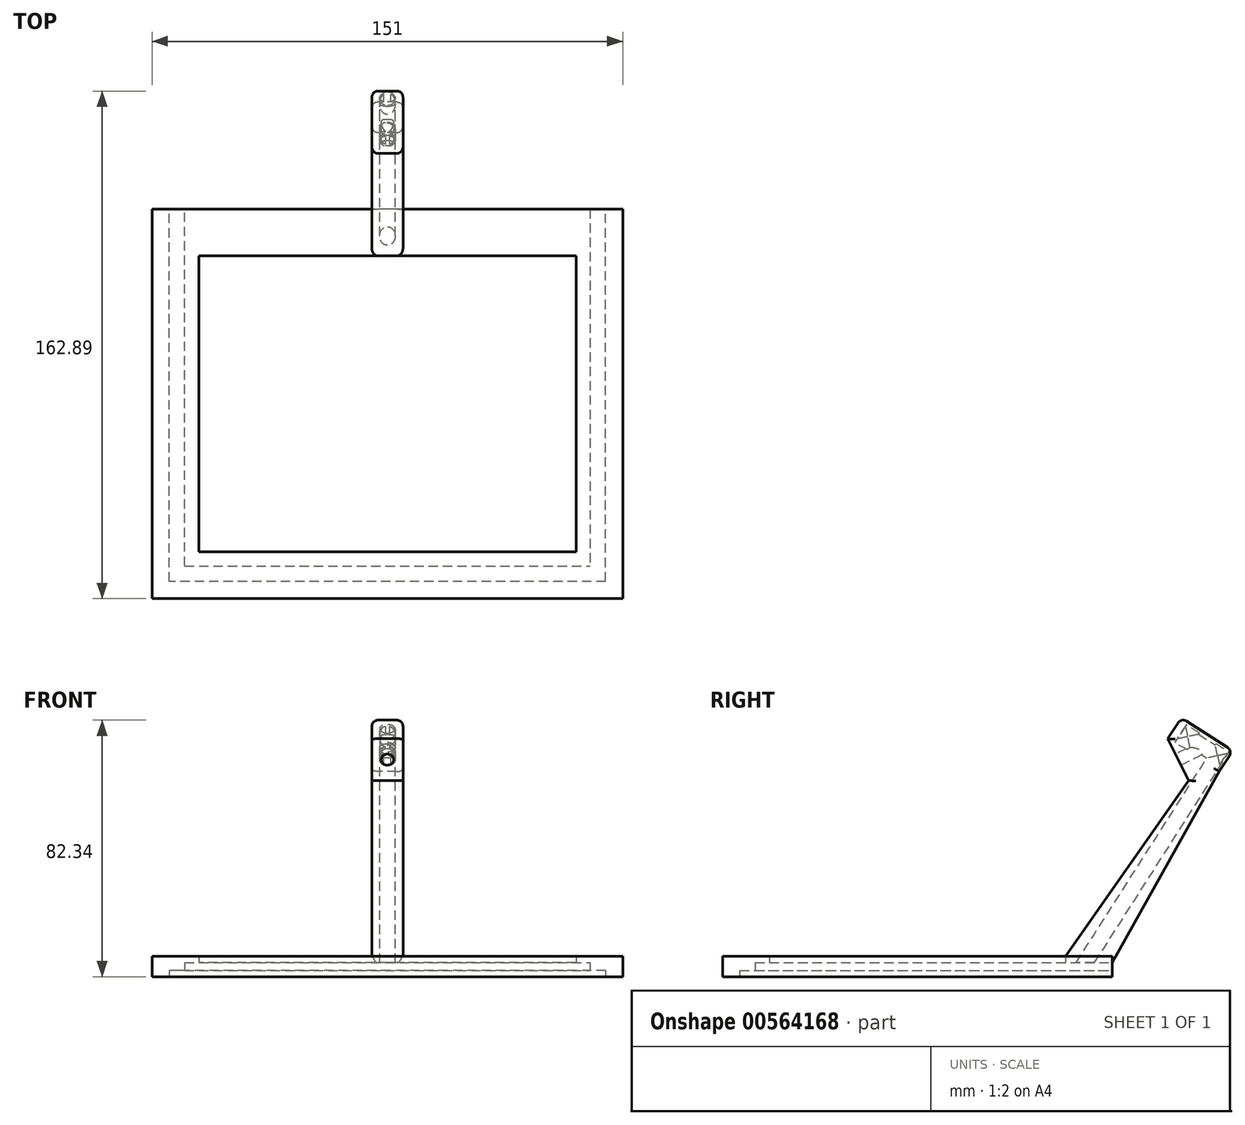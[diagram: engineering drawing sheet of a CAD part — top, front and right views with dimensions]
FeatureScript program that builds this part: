
annotation { "Feature Type Name" : "Feature", "Feature Type Description" : "" }
export const myFeature = defineFeature(function(context is Context, id is Id, definition is map)
    precondition{}
    {
        {
            var Q0;
            Q0=qCreatedBy(makeId("Top.planeOp"),FACE);
            var sketch = newSketch(context, id + "F0", { "sketchPlane" : qUnion([Q0])});
            skLineSegment(sketch, "E0.bottom", {"start": v(60.5, -47.5) * mm, "end": v(-60.5, -47.5) * mm});
            skLineSegment(sketch, "E0.top", {"start": v(60.5, 47.5) * mm, "end": v(-60.5, 47.5) * mm});
            skLineSegment(sketch, "E0.left", {"start": v(60.5, -47.5) * mm, "end": v(60.5, 47.5) * mm});
            skLineSegment(sketch, "E0.right", {"start": v(-60.5, -47.5) * mm, "end": v(-60.5, 47.5) * mm});
            skPoint(sketch, "E0.middle", {"position": v(0, 0) * mm});
            skLineSegment(sketch, "E1.bottom", {"start": v(75.5, -62.5) * mm, "end": v(-75.5, -62.5) * mm});
            skLineSegment(sketch, "E1.top", {"start": v(75.5, 62.5) * mm, "end": v(-75.5, 62.5) * mm});
            skLineSegment(sketch, "E1.left", {"start": v(75.5, -62.5) * mm, "end": v(75.5, 62.5) * mm});
            skLineSegment(sketch, "E1.right", {"start": v(-75.5, -62.5) * mm, "end": v(-75.5, 62.5) * mm});
            skSolve(sketch);
        }
        {
            var Q0;
            Q0=makeQuery(id+"F0.imprint","IMPRINT",FACE,{"disambiguationData":[TD([[makeQuery(id+"F0.imprint","IMPRINT",EDGE,{"derivedFrom":sQuery(id+"F0.wireOp",EDGE,"E0.bottom")}),1.0]])]});
            extrude(context, id + "F1", {"entities" : qUnion([Q0]), "depth" : 5 * mm, "offsetDistance" : 25 * mm});
        }
        {
            var Q0;
            Q0=makeQuery(id+"F1.opExtrude","CAP_FACE",FACE,{"disambiguationData":[OSD([sQuery(id+"F0.wireOp",EDGE,"E0.bottom"),sQuery(id+"F0.wireOp",EDGE,"E0.top"),sQuery(id+"F0.wireOp",EDGE,"E0.left"),sQuery(id+"F0.wireOp",EDGE,"E0.right"),sQuery(id+"F0.wireOp",EDGE,"E1.bottom"),sQuery(id+"F0.wireOp",EDGE,"E1.top"),sQuery(id+"F0.wireOp",EDGE,"E1.left"),sQuery(id+"F0.wireOp",EDGE,"E1.right")])],"isStart":true});
            var sketch = newSketch(context, id + "F2", { "sketchPlane" : qUnion([Q0])});
            skLineSegment(sketch, "E2.bottom", {"start": v(-65, 52) * mm, "end": v(65, 52) * mm});
            skLineSegment(sketch, "E2.top", {"start": v(-65, -52) * mm, "end": v(65, -52) * mm});
            skLineSegment(sketch, "E2.left", {"start": v(-65, 52) * mm, "end": v(-65, -52) * mm});
            skLineSegment(sketch, "E2.right", {"start": v(65, 52) * mm, "end": v(65, -52) * mm});
            skPoint(sketch, "E2.middle", {"position": v(0, 0) * mm});
            skSolve(sketch);
        }
        {
            var Q0;
            Q0=makeQuery(id+"F2.imprint","IMPRINT",FACE,{"disambiguationData":[TD([[makeQuery(id+"F2.imprint","IMPRINT",EDGE,{"derivedFrom":sQuery(id+"F2.wireOp",EDGE,"E2.bottom")}),-1.0]])]});
            extrude(context, id + "F3", {"entities" : qUnion([Q0]), "operationType" : NewBodyOperationType.REMOVE, "oppositeDirection" : true, "depth" : 3 * mm, "offsetDistance" : 25 * mm});
        }
        {
            var Q0;
            Q0=makeQuery(id+"F1.opExtrude","CAP_FACE",FACE,{"disambiguationData":[OSD([sQuery(id+"F0.wireOp",EDGE,"E0.bottom"),sQuery(id+"F0.wireOp",EDGE,"E0.top"),sQuery(id+"F0.wireOp",EDGE,"E0.left"),sQuery(id+"F0.wireOp",EDGE,"E0.right"),sQuery(id+"F0.wireOp",EDGE,"E1.bottom"),sQuery(id+"F0.wireOp",EDGE,"E1.top"),sQuery(id+"F0.wireOp",EDGE,"E1.left"),sQuery(id+"F0.wireOp",EDGE,"E1.right")])],"isStart":true});
            var sketch = newSketch(context, id + "F4", { "sketchPlane" : qUnion([Q0])});
            skLineSegment(sketch, "E3.bottom", {"start": v(75.5, 62.5) * mm, "end": v(-75.5, 62.5) * mm});
            skLineSegment(sketch, "E3.top", {"start": v(75.5, -62.5) * mm, "end": v(-75.5, -62.5) * mm});
            skLineSegment(sketch, "E3.left", {"start": v(75.5, 62.5) * mm, "end": v(75.5, -62.5) * mm});
            skLineSegment(sketch, "E3.right", {"start": v(-75.5, 62.5) * mm, "end": v(-75.5, -62.5) * mm});
            skPoint(sketch, "E3.middle", {"position": v(0, 0) * mm});
            skSolve(sketch);
        }
        {
            var Q0;
            Q0=makeQuery(id+"F3.boolean.opBoolean","COPY",FACE,{"derivedFrom":makeQuery(id+"F3.opExtrude","SWEPT_FACE",FACE,{"disambiguationData":[OSD([sQuery(id+"F2.wireOp",EDGE,"E2.top")])]})});
            var sketch = newSketch(context, id + "F5", { "sketchPlane" : qUnion([Q0])});
            skLineSegment(sketch, "E4.bottom", {"start": v(-65, 0) * mm, "end": v(65, 0) * mm});
            skLineSegment(sketch, "E4.top", {"start": v(-65, 3) * mm, "end": v(65, 3) * mm});
            skLineSegment(sketch, "E4.left", {"start": v(-65, 0) * mm, "end": v(-65, 3) * mm});
            skLineSegment(sketch, "E4.right", {"start": v(65, 0) * mm, "end": v(65, 3) * mm});
            skSolve(sketch);
        }
        {
            var Q0;
            Q0 = qSketchRegion(id + "F5", true);
            var Q1;
            Q1=makeQuery(id+"Fqpknaeqnkh5pSi_1.boolean.opBoolean","MERGE",FACE,{"derivedFrom":[makeQuery(id+"F1.opExtrude","SWEPT_FACE",FACE,{"disambiguationData":[OSD([sQuery(id+"F0.wireOp",EDGE,"E1.top")])]}),makeQuery(id+"Fqpknaeqnkh5pSi_1.opExtrude","SWEPT_FACE",FACE,{"disambiguationData":[OSD([sQuery(id+"F4.wireOp",EDGE,"E3.top")])]})]});
            extrude(context, id + "F6", {"entities" : qUnion([Q0]), "operationType" : NewBodyOperationType.REMOVE, "endBound" : BoundingType.UP_TO_SURFACE, "oppositeDirection" : true, "depth" : 25 * mm, "endBoundEntityFace" : qUnion([Q1]), "offsetDistance" : 25 * mm});
        }
        {
            var Q0;
            Q0=makeQuery(id+"F1.opExtrude","CAP_FACE",FACE,{"disambiguationData":[OSD([sQuery(id+"F0.wireOp",EDGE,"E0.bottom"),sQuery(id+"F0.wireOp",EDGE,"E0.top"),sQuery(id+"F0.wireOp",EDGE,"E0.left"),sQuery(id+"F0.wireOp",EDGE,"E0.right"),sQuery(id+"F0.wireOp",EDGE,"E1.bottom"),sQuery(id+"F0.wireOp",EDGE,"E1.top"),sQuery(id+"F0.wireOp",EDGE,"E1.left"),sQuery(id+"F0.wireOp",EDGE,"E1.right")])],"isStart":false});
            var sketch = newSketch(context, id + "F7", { "sketchPlane" : qUnion([Q0])});
            skPoint(sketch, "E5", {"position": v(0, 47.5) * mm});
            skLineSegment(sketch, "E6", {"start": v(0, 47.5) * mm, "end": v(0, 62.5) * mm});
            skSolve(sketch);
        }
        {
            var Q0;
            Q0=qCreatedBy(makeId("Right.planeOp"),FACE);
            var sketch = newSketch(context, id + "F8", { "sketchPlane" : qUnion([Q0])});
            skPoint(sketch, "E7", {"position": v(47.5, 5) * mm});
            skLineSegment(sketch, "E8", {"start": v(47.5, 5) * mm, "end": v(62.5, 5) * mm});
            skLineSegment(sketch, "E9", {"start": v(62.5, 5) * mm, "end": v(100, 69.95) * mm});
            skLineSegment(sketch, "E10", {"start": v(47.5, 5) * mm, "end": v(92.98, 69.95) * mm});
            skLineSegment(sketch, "E11", {"start": v(100, 69.95) * mm, "end": v(92.98, 69.95) * mm});
            skPoint(sketch, "E12", {"position": v(62.5, 3) * mm});
            skLineSegment(sketch, "E13", {"start": v(62.5, 3) * mm, "end": v(100, 69.95) * mm});
            skLineSegment(sketch, "E14", {"start": v(62.5, 5) * mm, "end": v(62.5, 3) * mm});
            skSolve(sketch);
        }
        {
            var Q0;
            Q0 = qSketchRegion(id + "F8", true);
            extrude(context, id + "F9", {"entities" : qUnion([Q0]), "operationType" : NewBodyOperationType.ADD, "endBound" : BoundingType.SYMMETRIC, "depth" : 10 * mm, "offsetDistance" : 25 * mm});
        }
        {
            var Q0;
            Q0=qCreatedBy(makeId("Right.planeOp"),FACE);
            var sketch = newSketch(context, id + "F10", { "sketchPlane" : qUnion([Q0])});
            skPoint(sketch, "E15", {"position": v(55, 5) * mm});
            skPoint(sketch, "E16", {"position": v(100, 69.95) * mm});
            skPoint(sketch, "E17", {"position": v(92.98, 69.95) * mm});
            skLineSegment(sketch, "E18", {"start": v(100, 69.95) * mm, "end": v(92.98, 69.95) * mm, "construction": true});
            skPoint(sketch, "E19", {"position": v(96.49, 69.95) * mm});
            skLineSegment(sketch, "E20", {"start": v(96.49, 69.95) * mm, "end": v(55, 5) * mm, "construction": true});
            skLineSegment(sketch, "E21", {"start": v(100, 69.95) * mm, "end": v(94.38, 73.54) * mm});
            skLineSegment(sketch, "E22", {"start": v(97.81, 63.7) * mm, "end": v(90.43, 68.42) * mm});
            skLineSegment(sketch, "E23", {"start": v(90.43, 68.42) * mm, "end": v(94.38, 73.54) * mm});
            skLineSegment(sketch, "E24", {"start": v(97.81, 63.7) * mm, "end": v(100, 69.95) * mm});
            skSolve(sketch);
        }
        {
            var Q0;
            Q0=makeQuery(id+"F10.imprint","IMPRINT",FACE,{"disambiguationData":[TD([[makeQuery(id+"F10.imprint","IMPRINT",EDGE,{"derivedFrom":sQuery(id+"F10.wireOp",EDGE,"E21")}),1.0]])]});
            extrude(context, id + "F11", {"entities" : qUnion([Q0]), "operationType" : NewBodyOperationType.REMOVE, "endBound" : BoundingType.SYMMETRIC, "oppositeDirection" : true, "depth" : 25 * mm, "offsetDistance" : 25 * mm});
        }
        {
            var Q0;
            Q0=makeQuery(id+"F11.boolean.opBoolean","COPY",FACE,{"derivedFrom":makeQuery(id+"F11.opExtrude","SWEPT_FACE",FACE,{"disambiguationData":[OSD([sQuery(id+"F10.wireOp",EDGE,"E22")])]})});
            var sketch = newSketch(context, id + "F12", { "sketchPlane" : qUnion([Q0])});
            skCircle(sketch, "E25", {"center": v(0, 43.79) * mm, "radius": 2.5 * mm});
            skPoint(sketch, "E25.centerSnap0", {"position": v(-5, 43.79) * mm});
            skPoint(sketch, "E25.centerSnap1", {"position": v(0, 40.59) * mm});
            skSolve(sketch);
        }
        {
            var Q0;
            Q0=makeQuery(id+"F11.boolean.opBoolean","COPY",FACE,{"derivedFrom":makeQuery(id+"F11.opExtrude","SWEPT_FACE",FACE,{"disambiguationData":[OSD([sQuery(id+"F10.wireOp",EDGE,"E22")])]})});
            var sketch = newSketch(context, id + "F13", { "sketchPlane" : qUnion([Q0])});
            skLineSegment(sketch, "E26.bottom", {"start": v(-5, 47) * mm, "end": v(5, 47) * mm});
            skLineSegment(sketch, "E26.top", {"start": v(-5, 27.42) * mm, "end": v(5, 27.42) * mm});
            skLineSegment(sketch, "E26.left", {"start": v(-5, 47) * mm, "end": v(-5, 27.42) * mm});
            skLineSegment(sketch, "E26.right", {"start": v(5, 47) * mm, "end": v(5, 27.42) * mm});
            skSolve(sketch);
        }
        {
            var Q0;
            Q0 = qSketchRegion(id + "F13", true);
            extrude(context, id + "F14", {"entities" : qUnion([Q0]), "operationType" : NewBodyOperationType.ADD, "depth" : 8 * mm, "offsetDistance" : 25 * mm});
        }
        {
            var Q0;
            {var subQ0=sQuery(id+"F13.wireOp",EDGE,"E26.top");var subQ1=sQuery(id+"F8.wireOp",EDGE,"E10");var subQ6=sQuery(id+"F13.wireOp",EDGE,"E26.left");var subQ7=sQuery(id+"F13.wireOp",EDGE,"E26.right");Q0=makeQuery(id+"F14.boolean.opBoolean","SPLIT",FACE,{"disambiguationData":[TD([makeQuery(id+"F9.opExtrude","SWEPT_FACE",FACE,{"disambiguationData":[OSD([subQ1])]})])],"derivedFrom":makeQuery(id+"F14.opExtrude","CAP_FACE",FACE,{"disambiguationData":[OSD([sQuery(id+"F13.wireOp",EDGE,"E26.bottom"),subQ0,subQ6,subQ7])],"isStart":true})});}
            var sketch = newSketch(context, id + "F15", { "sketchPlane" : qUnion([Q0])});
            skPoint(sketch, "E27", {"position": v(0, -32.42) * mm});
            skCircle(sketch, "E28", {"center": v(0, -32.42) * mm, "radius": 2.5 * mm});
            skSolve(sketch);
        }
        {
            var Q0;
            Q0=makeQuery(id+"F14.opExtrude","SWEPT_FACE",FACE,{"disambiguationData":[OSD([sQuery(id+"F13.wireOp",EDGE,"E26.bottom")])]});
            var sketch = newSketch(context, id + "F16", { "sketchPlane" : qUnion([Q0])});
            skCircle(sketch, "E29", {"center": v(0, 110.34) * mm, "radius": 2.5 * mm});
            skPoint(sketch, "E29.centerSnap0", {"position": v(5, 110.34) * mm});
            skSolve(sketch);
        }
        {
            var Q0;
            Q0 = qSketchRegion(id + "F16", true);
            extrude(context, id + "F17", {"entities" : qUnion([Q0]), "operationType" : NewBodyOperationType.REMOVE, "oppositeDirection" : true, "depth" : 17 * mm, "offsetDistance" : 25 * mm});
        }
        {
            var Q0;
            Q0=makeQuery(id+"F14.opExtrude","SWEPT_FACE",FACE,{"disambiguationData":[OSD([sQuery(id+"F13.wireOp",EDGE,"E26.bottom")])]});
            var sketch = newSketch(context, id + "F18", { "sketchPlane" : qUnion([Q0])});
            skLineSegment(sketch, "E30.bottom", {"start": v(5, 114.34) * mm, "end": v(-5, 114.34) * mm});
            skLineSegment(sketch, "E30.top", {"start": v(5, 106.34) * mm, "end": v(-5, 106.34) * mm});
            skLineSegment(sketch, "E30.left", {"start": v(5, 114.34) * mm, "end": v(5, 106.34) * mm});
            skLineSegment(sketch, "E30.right", {"start": v(-5, 114.34) * mm, "end": v(-5, 106.34) * mm});
            skSolve(sketch);
        }
        {
            var Q0;
            Q0 = qSketchRegion(id + "F18", true);
            extrude(context, id + "F19", {"entities" : qUnion([Q0]), "operationType" : NewBodyOperationType.ADD, "oppositeDirection" : true, "depth" : 1 * mm, "offsetDistance" : 25 * mm});
        }
        {
            var Q0;
            Q0=makeQuery(id+"F12.imprint","IMPRINT",FACE,{"disambiguationData":[TD([[makeQuery(id+"F12.imprint","IMPRINT",EDGE,{"derivedFrom":sQuery(id+"F12.wireOp",EDGE,"E25")}),1.0]])]});
            var Q1;
            Q1=makeQuery(id+"F6.boolean.opBoolean","MERGE",FACE,{"derivedFrom":[makeQuery(id+"F3.boolean.opBoolean","COPY",FACE,{"derivedFrom":makeQuery(id+"F3.opExtrude","CAP_FACE",FACE,{"disambiguationData":[OSD([sQuery(id+"F0.wireOp",EDGE,"E0.bottom"),sQuery(id+"F0.wireOp",EDGE,"E0.top"),sQuery(id+"F0.wireOp",EDGE,"E0.left"),sQuery(id+"F0.wireOp",EDGE,"E0.right"),sQuery(id+"F2.wireOp",EDGE,"E2.bottom"),sQuery(id+"F2.wireOp",EDGE,"E2.top"),sQuery(id+"F2.wireOp",EDGE,"E2.left"),sQuery(id+"F2.wireOp",EDGE,"E2.right")])],"isStart":false})}),makeQuery(id+"F6.opExtrude","SWEPT_FACE",FACE,{"disambiguationData":[OSD([sQuery(id+"F5.wireOp",EDGE,"E4.top")])]})]});
            extrude(context, id + "F20", {"entities" : qUnion([Q0]), "operationType" : NewBodyOperationType.REMOVE, "endBound" : BoundingType.UP_TO_SURFACE, "oppositeDirection" : true, "depth" : 25 * mm, "endBoundEntityFace" : qUnion([Q1]), "offsetDistance" : 25 * mm, "hasSecondDirection" : true, "secondDirectionOppositeDirection" : false, "secondDirectionDepth" : 7 * mm});
        }
        {
            var Q0;
            Q0 = qSketchRegion(id + "F15", true);
            extrude(context, id + "F21", {"entities" : qUnion([Q0]), "operationType" : NewBodyOperationType.REMOVE, "oppositeDirection" : true, "depth" : 7 * mm, "hasOffset" : true, "offsetDistance" : 2 * mm});
        }
        {
            var Q0;
            Q0=qCreatedBy(makeId("Right.planeOp"),FACE);
            var sketch = newSketch(context, id + "F22", { "sketchPlane" : qUnion([Q0])});
            skPoint(sketch, "E31", {"position": v(-47.5, 5) * mm});
            skPoint(sketch, "E32", {"position": v(47.5, 5) * mm});
            skPoint(sketch, "E33", {"position": v(85.84, 71.35) * mm});
            skLineSegment(sketch, "E34", {"start": v(-47.5, 5) * mm, "end": v(85.84, 71.35) * mm, "construction": true});
            skLineSegment(sketch, "E35", {"start": v(47.5, 5) * mm, "end": v(28.64, 42.9) * mm, "construction": true});
            skLineSegment(sketch, "E36", {"start": v(28.64, 42.9) * mm, "end": v(15.94, 68.42) * mm, "construction": true});
            skLineSegment(sketch, "E37", {"start": v(80.35, 74.86) * mm, "end": v(87.14, 61.22) * mm});
            skLineSegment(sketch, "E38", {"start": v(87.14, 61.22) * mm, "end": v(92.1, 68.27) * mm});
            skLineSegment(sketch, "E39", {"start": v(92.1, 68.27) * mm, "end": v(80.35, 74.86) * mm});
            skSolve(sketch);
        }
        {
            var Q0;
            Q0 = qSketchRegion(id + "F22", true);
            extrude(context, id + "F23", {"entities" : qUnion([Q0]), "operationType" : NewBodyOperationType.ADD, "endBound" : BoundingType.SYMMETRIC, "depth" : 10 * mm, "offsetDistance" : 25 * mm});
        }
        {
            var Q0;
            Q0=makeQuery(id+"F23.opExtrude","SWEPT_FACE",FACE,{"disambiguationData":[OSD([sQuery(id+"F22.wireOp",EDGE,"E37")])]});
            var sketch = newSketch(context, id + "F24", { "sketchPlane" : qUnion([Q0])});
            skCircle(sketch, "E40", {"center": v(0, 23.73) * mm, "radius": 2 * mm});
            skPoint(sketch, "E40.centerSnap0", {"position": v(-5, 23.73) * mm});
            skPoint(sketch, "E40.centerSnap1", {"position": v(0, 31.22) * mm});
            skSolve(sketch);
        }
        {
            var Q0;
            Q0=makeQuery(id+"F24.imprint","IMPRINT",FACE,{"disambiguationData":[TD([[makeQuery(id+"F24.imprint","IMPRINT",EDGE,{"derivedFrom":sQuery(id+"F24.wireOp",EDGE,"E40")}),1.0]])]});
            extrude(context, id + "F25", {"entities" : qUnion([Q0]), "operationType" : NewBodyOperationType.REMOVE, "endBound" : BoundingType.UP_TO_NEXT, "oppositeDirection" : true, "depth" : 25 * mm, "offsetDistance" : 25 * mm});
        }
        {
            var Q0;
            Q0=makeQuery(id+"F14.opExtrude","CAP_EDGE",EDGE,{"disambiguationData":[OSD([sQuery(id+"F13.wireOp",EDGE,"E26.bottom")])],"isStart":false});
            var Q1;
            Q1=makeQuery(id+"F14.opExtrude","CAP_EDGE",EDGE,{"disambiguationData":[OSD([sQuery(id+"F13.wireOp",EDGE,"E26.top")])],"isStart":false});
            var Q2;
            Q2=makeQuery(id+"F14.opExtrude","CAP_EDGE",EDGE,{"disambiguationData":[OSD([sQuery(id+"F13.wireOp",EDGE,"E26.left")])],"isStart":false});
            var Q3;
            Q3=makeQuery(id+"F14.opExtrude","CAP_EDGE",EDGE,{"disambiguationData":[OSD([sQuery(id+"F13.wireOp",EDGE,"E26.right")])],"isStart":false});
            var Q4;
            Q4=makeQuery(id+"F14.opExtrude","SWEPT_EDGE",EDGE,{"disambiguationData":[OSD([sQuery(id+"F13.wireOp",EDGE,"E26.top"),sQuery(id+"F13.wireOp",EDGE,"E26.left")])]});
            var Q5;
            Q5=makeQuery(id+"F23.opExtrude","CAP_EDGE",EDGE,{"disambiguationData":[OSD([sQuery(id+"F22.wireOp",EDGE,"E37")])],"isStart":true});
            var Q6;
            Q6=makeQuery(id+"F14.opExtrude","SWEPT_EDGE",EDGE,{"disambiguationData":[OSD([sQuery(id+"F13.wireOp",EDGE,"E26.bottom"),sQuery(id+"F13.wireOp",EDGE,"E26.left")])]});
            var Q7;
            Q7=makeQuery(id+"F14.opExtrude","SWEPT_EDGE",EDGE,{"disambiguationData":[OSD([sQuery(id+"F13.wireOp",EDGE,"E26.bottom"),sQuery(id+"F13.wireOp",EDGE,"E26.right")])]});
            var Q8;
            Q8=makeQuery(id+"F9.opExtrude","CAP_EDGE",EDGE,{"disambiguationData":[OSD([sQuery(id+"F8.wireOp",EDGE,"E13")])],"isStart":false});
            var Q9;
            Q9=makeQuery(id+"F9.opExtrude","CAP_EDGE",EDGE,{"disambiguationData":[OSD([sQuery(id+"F8.wireOp",EDGE,"E13")])],"isStart":true});
            var Q10;
            Q10=makeQuery(id+"F9.opExtrude","CAP_EDGE",EDGE,{"disambiguationData":[OSD([sQuery(id+"F8.wireOp",EDGE,"E10")])],"isStart":true});
            var Q11;
            Q11=makeQuery(id+"F14.opExtrude","SWEPT_EDGE",EDGE,{"disambiguationData":[OSD([sQuery(id+"F13.wireOp",EDGE,"E26.top"),sQuery(id+"F13.wireOp",EDGE,"E26.right")])]});
            var Q12;
            Q12=makeQuery(id+"F23.opExtrude","CAP_EDGE",EDGE,{"disambiguationData":[OSD([sQuery(id+"F22.wireOp",EDGE,"E37")])],"isStart":false});
            var Q13;
            Q13=makeQuery(id+"F9.opExtrude","CAP_EDGE",EDGE,{"disambiguationData":[OSD([sQuery(id+"F8.wireOp",EDGE,"E10")])],"isStart":false});
            fillet(context, id + "F26", {"entities" : qUnion([Q0, Q1, Q2, Q3, Q4, Q5, Q6, Q7, Q8, Q9, Q10, Q11, Q12, Q13]), "radius" : 2 * mm, "tangentPropagation" : true, "allowEdgeOverflow" : false});
        }
        {
            var Q0;
            Q0=makeQuery(id+"F4.imprint","IMPRINT",FACE,{"disambiguationData":[TD([[makeQuery(id+"F4.imprint","IMPRINT",EDGE,{"derivedFrom":sQuery(id+"F4.wireOp",EDGE,"E3.bottom")}),1.0]])]});
            var sketch = newSketch(context, id + "F27", { "sketchPlane" : qUnion([Q0])});
            skLineSegment(sketch, "E41.bottom", {"start": v(70, 57) * mm, "end": v(-70, 57) * mm});
            skLineSegment(sketch, "E41.top", {"start": v(70, -62.5) * mm, "end": v(-70, -62.5) * mm});
            skLineSegment(sketch, "E41.left", {"start": v(70, 57) * mm, "end": v(70, -62.5) * mm});
            skLineSegment(sketch, "E41.right", {"start": v(-70, 57) * mm, "end": v(-70, -62.5) * mm});
            skSolve(sketch);
        }
        {
            var Q0;
            Q0=makeQuery(id+"F27.imprint","IMPRINT",FACE,{"disambiguationData":[TD([[makeQuery(id+"F27.imprint","IMPRINT",EDGE,{"derivedFrom":sQuery(id+"F27.wireOp",EDGE,"E41.bottom")}),1.0]])]});
            extrude(context, id + "F28", {"entities" : qUnion([Q0]), "operationType" : NewBodyOperationType.REMOVE, "oppositeDirection" : true, "depth" : 0.5 * mm, "offsetDistance" : 25 * mm});
        }
        {
            var Q0;
            Q0=makeQuery(id+"F4.imprint","IMPRINT",FACE,{"disambiguationData":[TD([[makeQuery(id+"F4.imprint","IMPRINT",EDGE,{"derivedFrom":sQuery(id+"F4.wireOp",EDGE,"E3.bottom")}),1.0]])]});
            var sketch = newSketch(context, id + "F29", { "sketchPlane" : qUnion([Q0])});
            skPoint(sketch, "E42", {"position": v(70, -62.5) * mm});
            skPoint(sketch, "E43", {"position": v(75.5, -62.5) * mm});
            skPoint(sketch, "E44", {"position": v(75.5, 62.5) * mm});
            skPoint(sketch, "E45", {"position": v(70, 57) * mm});
            skPoint(sketch, "E46", {"position": v(-75.5, 62.5) * mm});
            skPoint(sketch, "E47", {"position": v(-70, 57) * mm});
            skPoint(sketch, "E48", {"position": v(-70, -62.5) * mm});
            skPoint(sketch, "E49", {"position": v(-75.5, -62.5) * mm});
            skLineSegment(sketch, "E50", {"start": v(70, -62.5) * mm, "end": v(75.5, -62.5) * mm});
            skLineSegment(sketch, "E51", {"start": v(75.5, 62.5) * mm, "end": v(-75.5, 62.5) * mm});
            skLineSegment(sketch, "E52", {"start": v(-75.5, -62.5) * mm, "end": v(-70, -62.5) * mm});
            skLineSegment(sketch, "E53", {"start": v(-70, 57) * mm, "end": v(70, 57) * mm});
            skLineSegment(sketch, "E54", {"start": v(70, -62.5) * mm, "end": v(70, 57) * mm});
            skLineSegment(sketch, "E55", {"start": v(75.5, -62.5) * mm, "end": v(75.5, 62.5) * mm});
            skLineSegment(sketch, "E56", {"start": v(-70, -62.5) * mm, "end": v(-70, 57) * mm});
            skLineSegment(sketch, "E57", {"start": v(-75.5, -62.5) * mm, "end": v(-75.5, 62.5) * mm});
            skSolve(sketch);
        }
        {
            var Q0;
            Q0=makeQuery(id+"F29.imprint","IMPRINT",FACE,{"disambiguationData":[TD([[makeQuery(id+"F29.imprint","IMPRINT",EDGE,{"derivedFrom":sQuery(id+"F29.wireOp",EDGE,"E50")}),-1.0]])]});
            extrude(context, id + "F30", {"entities" : qUnion([Q0]), "operationType" : NewBodyOperationType.ADD, "depth" : 1.5 * mm, "offsetDistance" : 25 * mm});
        }
    });
